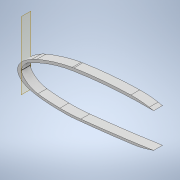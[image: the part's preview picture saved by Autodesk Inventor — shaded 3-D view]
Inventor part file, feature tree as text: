
AUTODESK INVENTOR PART (.ipt)
format: ipt  version: 2022.1 (Build 261234020, 234B)  size: 624,128 bytes
history: native  units: mm
features: sketch x8, extrude x7, thicken_offset x4, fillet x4, projected_geometry x4, shell x1, plane x1, other x1
ambient origin geometry x8: Origin, YZ Plane, XZ Plane, XY Plane, X Axis, Y Axis, Z Axis, Center Point
bodies: Solid1 (feature_tree)
feature tree (30):
  extrude  "Extrusion1"  Depth=10.0mm
  shell  "Shell1"  Thickness=1.0mm
  thicken_offset  "Thicken1"
  extrude  "Extrusion27"  TaperAngle=0.0deg  [1 undecoded]
  thicken_offset  "Thicken3"
  extrude  "Extrusion29"  Depth=20.0mm
  plane  "Work Plane5"
  other  "Bend Part2"
  thicken_offset  "Thicken5"
  extrude  "Extrusion30"  Depth=10.0mm TaperAngle=0.0deg
  extrude  "Extrusion31"  Depth=10.0mm
  fillet  "Fillet6"  Radius=1.0mm
  fillet  "Fillet8"  Radius=150.0mm
  thicken_offset  "Thicken6"
  extrude  "Extrusion32"  Depth=10.0mm TaperAngle=0.0deg
  fillet  "Fillet9"  Radius=150.0mm
  extrude  "Extrusion33"  Depth=550.0mm
  fillet  "Fillet10"  Radius=130.0mm
  sketch  "Sketch3"  dims[d0=10.0mm d1=0.0mm d2=3.0mm d159=1.0mm d160=2.0mm]
  sketch  "Sketch48"  dims[d236=190.0mm d237=0.0mm d238=0.0mm]
  sketch  "Sketch55"  dims[d249=2.0mm d250=1.0mm d254=20.0mm]
  projected_geometry  "Projected Loop32"
  sketch  "Sketch57"  dims[d255=8.0mm d256=10.0mm d257=0.0mm]
  sketch  "Sketch58"  dims[d262=10.0mm d263=0.523599mm d264=1.0mm d265=1.0mm d268=150.0mm]
  projected_geometry  "Projected Loop34"
  sketch  "Sketch59"  dims[d269=6.0mm d270=10.0mm d271=0.0mm d272=150.0mm]
  sketch  "Sketch60"  dims[d273=100.0mm d274=0.0mm d275=550.0mm d276=130.0mm]
  projected_geometry  "Projected Loop35"
  sketch  "Sketch61"  dims[d277=9.0mm d278=2000.0mm d279=200.0mm d281=150.0mm d282=2.5mm d283=2.5mm d284=2.5mm d285=2.5mm d286=10.0mm d287=0.0mm d288=100.0mm d289=10.0mm d290=0.0mm d291=60.0mm]
  projected_geometry  "Projected Loop36"
note: 1 required parameter value undecoded (feature->parameter linkage not recoverable at this tier; creation-order binding heuristic only, values carry confidence <= 0.55)
